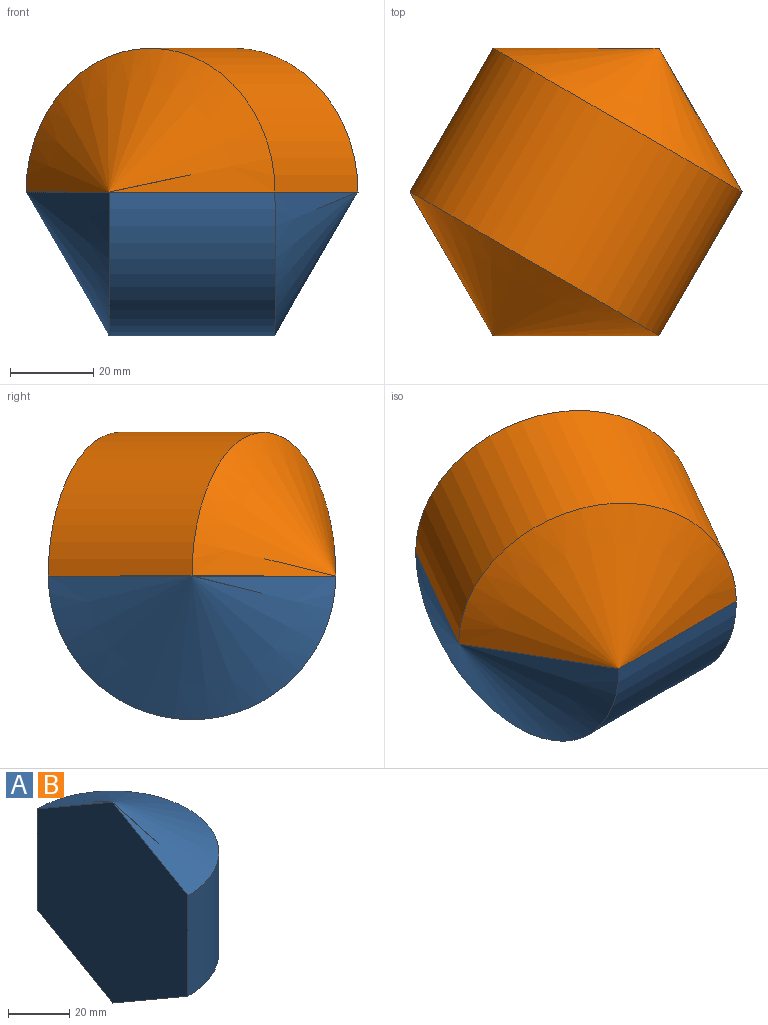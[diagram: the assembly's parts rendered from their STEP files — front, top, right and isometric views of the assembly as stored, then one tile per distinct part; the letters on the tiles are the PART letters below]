
ASSEMBLY  parts=2 mates=1
PART A: 4 faces, bbox 34.6x69.3x80 mm
  f0: cone r=0mm half-angle=60deg, axis (0,0,1), area 2176.6mm2, adj f1,f3
  f1: cylinder r=34.64mm len=69.28mm, axis (0,0,1), area 4353.1mm2, adj f0,f2,f3
  f2: cone r=34.64mm half-angle=60deg, axis (0,0,-1), area 2176.6mm2, adj f1,f3
  f3: plane 80x69.28mm, normal (-1,0,0), area 4156.9mm2, adj f0,f1,f2
PART B: same geometry as A
PLACE A rot(axis=(0,1,0),90deg) t=(0,0,0)mm fixed
PLACE B rot(axis=(0.45,-0.77,0.45),104.5deg) t=(0,0,0)mm
MATE fastened B.f3 <-> A.f3  axis (0,0,-1) through (0,0,0)mm
